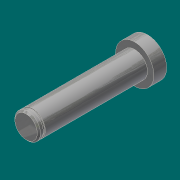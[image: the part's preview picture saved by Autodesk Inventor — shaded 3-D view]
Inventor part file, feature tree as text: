
AUTODESK INVENTOR PART (.ipt)
format: ipt  version: 2017 (Build 210142000, 142)  size: 166,400 bytes
history: native  units: in
note: dims shown in document units (in); Inventor stores cm internally (conversion verified against a paired STEP export)
features: extrude x5, sketch x5, chamfer x1
ambient origin geometry x8: Origin, YZ Plane, XZ Plane, XY Plane, X Axis, Y Axis, Z Axis, Center Point
bodies: Solid1 (feature_tree)
feature tree (11):
  extrude  "Extrusion1"  Depth=0.25in TaperAngle=0.0deg
  extrude  "Extrusion2"  Depth=2.0in TaperAngle=0.0deg
  extrude  "Extrusion3"  Depth=0.04in TaperAngle=0.0deg
  extrude  "Extrusion4"  Depth=0.125in TaperAngle=45.0deg
  chamfer  "Chamfer1"  Distance=0.125in
  extrude  "Extrusion5"  [1 undecoded]
  sketch  "Sketch1"  dims[d0=0.75in d1=0.25in d2=0.0in]
  sketch  "Sketch2"  dims[d3=0.5in d4=2.0in d5=0.0in]
  sketch  "Sketch3"  dims[d6=0.4688in d7=0.04in d8=0.0in]
  sketch  "Sketch4"  dims[d9=0.085in d10=0.0in d11=0.0312in d12=0.125in d13=45.0deg]
  sketch  "Sketch5"  dims[d14=0.25in d15=0.125in d16=0.0in]
note: 1 required parameter value undecoded (feature->parameter linkage not recoverable at this tier; creation-order binding heuristic only, values carry confidence <= 0.55)
